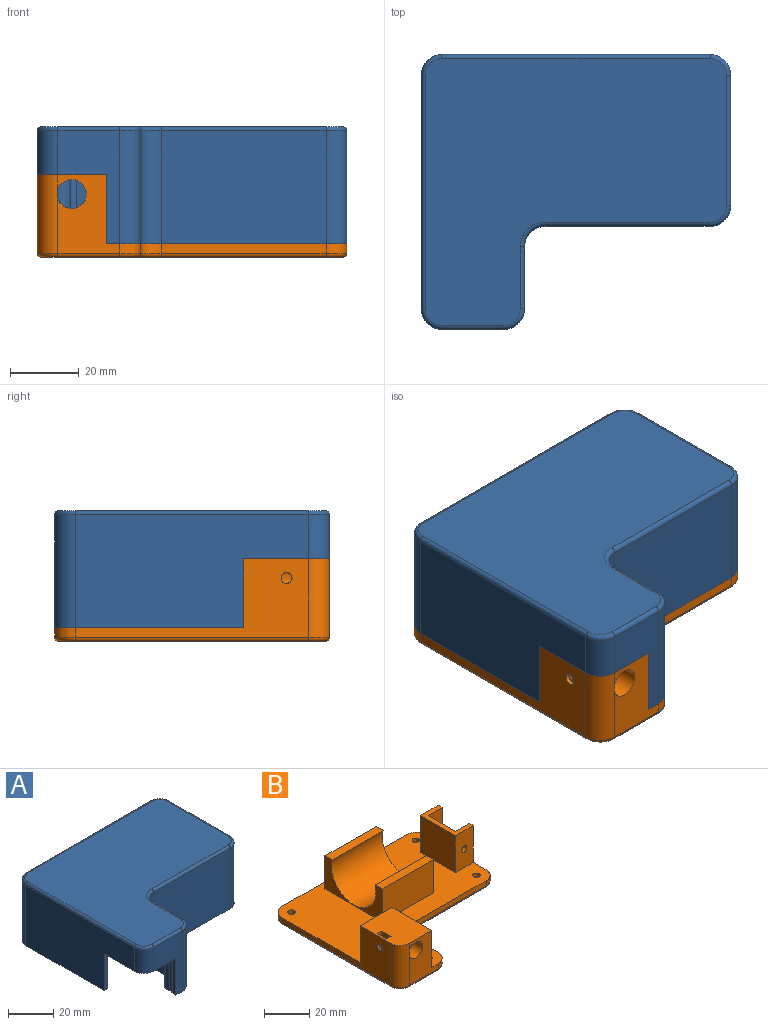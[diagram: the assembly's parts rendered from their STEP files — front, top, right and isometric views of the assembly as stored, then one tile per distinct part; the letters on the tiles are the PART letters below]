
ASSEMBLY  parts=2 mates=1
PART A: 66 faces, bbox 91x81x34 mm
  f0: plane 85.2x75.2mm, normal (0,0,-1), area 3833.6mm2, adj f15,f16,f17,f18,f19,f22,f23,f24
  f1: plane 48x32.8mm, normal (0,-1,0), area 1574.4mm2, adj f8,f13,f30,f64
  f2: plane 38x32.8mm, normal (1,0,0), area 806.4mm2, adj f8,f9,f14,f21,f28,f30,f45,f60
  f3: plane 78x32.8mm, normal (0,1,0), area 2558.4mm2, adj f9,f10,f21,f56
  f4: plane 68x32.8mm, normal (-1,0,0), area 1850.4mm2, adj f10,f11,f20,f21,f41,f55
  f5: plane 32.8x18mm, normal (0,-1,0), area 310.4mm2, adj f11,f12,f29,f30,f41,f59
  f6: plane 32.8x18mm, normal (1,0,0), area 590.4mm2, adj f12,f13,f30,f63
  f7: plane 87.6x77.6mm, normal (0,0,1), area 4984.2mm2, adj f54,f55,f56,f57,f58,f59,f60,f61
  f8: cylinder r=6mm len=32.8mm, axis (0,0,1), area 309.1mm2, adj f1,f2,f30,f62
  f9: cylinder r=6mm len=32.8mm, axis (0,0,-1), area 309.1mm2, adj f2,f3,f21,f58
  f10: cylinder r=6mm len=32.8mm, axis (0,0,1), area 309.1mm2, adj f3,f4,f21,f54
  f11: cylinder r=6mm len=12.8mm, axis (0,0,-1), area 120.6mm2, adj f4,f5,f41,f57
  f12: cylinder r=6mm len=32.8mm, axis (0,0,1), area 309.1mm2, adj f5,f6,f30,f61
  f13: cylinder r=6mm len=32.8mm, axis (0,0,-1), area 309.1mm2, adj f1,f6,f30,f65
  f14: plane 20x2.4mm, normal (0,-1,0), area 48mm2, adj f2,f15,f21,f45
  f15: plane 30x2.63mm, normal (-1,0,0), area 79mm2, adj f0,f14,f21,f31,f44
  f16: cylinder r=3.6mm len=30mm, axis (0,0,1), area 232.2mm2, adj f0,f21,f31,f32
  f17: plane 67.27x30mm, normal (0,-1,0), area 2018mm2, adj f0,f21,f32,f33
  f18: cylinder r=3.6mm len=30mm, axis (0,0,1), area 232.2mm2, adj f0,f21,f33,f34
  f19: plane 43.63x30mm, normal (1,0,0), area 1309mm2, adj f0,f20,f21,f34,f39
  f20: plane 20x2.4mm, normal (0,-1,0), area 48mm2, adj f4,f19,f21,f41
  f21: plane 90x55mm, normal (0,0,-1), area 446mm2, adj f2,f3,f4,f9,f10,f14,f15,f16
  f22: cylinder r=3.6mm len=30mm, axis (0,0,1), area 240.8mm2, adj f0,f30,f35,f38
  f23: plane 30x12.63mm, normal (-1,0,0), area 379mm2, adj f0,f24,f30,f38
  f24: cylinder r=8.4mm len=30mm, axis (0,0,1), area 395.8mm2, adj f0,f23,f25,f30
  f25: plane 42.63x30mm, normal (0,1,0), area 1279mm2, adj f0,f24,f30,f37
  f26: cylinder r=3.6mm len=30mm, axis (0,0,1), area 232.2mm2, adj f0,f30,f36,f37
  f27: plane 30x2.63mm, normal (-1,0,0), area 79mm2, adj f0,f28,f30,f36,f42
  f28: plane 20x2.4mm, normal (0,1,0), area 48mm2, adj f2,f27,f30,f45
  f29: plane 20x2.4mm, normal (-1,0,0), area 48mm2, adj f5,f30,f35,f41
  f30: plane 70x44mm, normal (0,0,-1), area 335.6mm2, adj f1,f2,f5,f6,f8,f12,f13,f22
  f31: cylinder r=2mm len=30mm, axis (0,0,1), area 111.6mm2, adj f0,f15,f16,f21
  f32: cylinder r=2mm len=30mm, axis (0,0,1), area 111.6mm2, adj f0,f16,f17,f21
  f33: cylinder r=2mm len=30mm, axis (0,0,1), area 111.6mm2, adj f0,f17,f18,f21
  f34: cylinder r=2mm len=30mm, axis (0,0,1), area 111.6mm2, adj f0,f18,f19,f21
  f35: cylinder r=2mm len=30mm, axis (0,0,-1), area 76.9mm2, adj f0,f22,f29,f30,f40
  f36: cylinder r=2mm len=30mm, axis (0,0,1), area 111.6mm2, adj f0,f26,f27,f30
  f37: cylinder r=2mm len=30mm, axis (0,0,1), area 111.6mm2, adj f0,f25,f26,f30
  f38: cylinder r=2mm len=30mm, axis (0,0,1), area 111.6mm2, adj f0,f22,f23,f30
  f39: plane 17.6x10mm, normal (0,1,0), area 176mm2, adj f0,f19,f40,f41
  f40: plane 22.6x10mm, normal (1,0,0), area 226mm2, adj f0,f35,f39,f41
  f41: plane 25x20mm, normal (0,0,-1), area 492.3mm2, adj f4,f5,f11,f20,f29,f39,f40
  f42: plane 10x8.8mm, normal (0,-1,0), area 88mm2, adj f0,f27,f43,f45
  f43: plane 22x10mm, normal (-1,0,0), area 220mm2, adj f0,f42,f44,f45
  f44: plane 10x8.8mm, normal (0,1,0), area 88mm2, adj f0,f15,f43,f45
  f45: plane 22x11.2mm, normal (0,0,-1), area 246.4mm2, adj f2,f14,f28,f42,f43,f44
  f46: cylinder r=1.1mm len=18mm, axis (0,0,-1), area 124.4mm2, adj f30,f47
  f47: cone r=0mm half-angle=59deg, axis (0,0,-1), area 4.4mm2, adj f46
  f48: cylinder r=1.1mm len=18mm, axis (0,0,-1), area 124.4mm2, adj f21,f49
  f49: cone r=0mm half-angle=59deg, axis (0,0,-1), area 4.4mm2, adj f48
  f50: cylinder r=1.1mm len=18mm, axis (0,0,-1), area 124.4mm2, adj f30,f51
  f51: cone r=0mm half-angle=59deg, axis (0,0,-1), area 4.4mm2, adj f50
  f52: cylinder r=1.1mm len=18mm, axis (0,0,-1), area 124.4mm2, adj f21,f53
  f53: cone r=0mm half-angle=59deg, axis (0,0,-1), area 4.4mm2, adj f52
  f54: torus R=4.8mm, axis (0,0,1), area 16.5mm2, adj f7,f10,f55,f56
  f55: cylinder r=1.2mm len=68mm, axis (0,1,0), area 128.2mm2, adj f4,f7,f54,f57
  f56: cylinder r=1.2mm len=78mm, axis (1,0,0), area 147mm2, adj f3,f7,f54,f58
  f57: torus R=4.8mm, axis (0,0,1), area 16.5mm2, adj f7,f11,f55,f59
  f58: torus R=4.8mm, axis (0,0,1), area 16.5mm2, adj f7,f9,f56,f60
  f59: cylinder r=1.2mm len=18mm, axis (-1,0,0), area 33.9mm2, adj f5,f7,f57,f61
  f60: cylinder r=1.2mm len=38mm, axis (0,-1,0), area 71.6mm2, adj f2,f7,f58,f62
  f61: torus R=4.8mm, axis (0,0,1), area 16.5mm2, adj f7,f12,f59,f63
  f62: torus R=4.8mm, axis (0,0,1), area 16.5mm2, adj f7,f8,f60,f64
  f63: cylinder r=1.2mm len=18mm, axis (0,-1,0), area 33.9mm2, adj f6,f7,f61,f65
  f64: cylinder r=1.2mm len=48mm, axis (-1,0,0), area 90.5mm2, adj f1,f7,f62,f65
  f65: torus R=7.2mm, axis (0,0,1), area 19.1mm2, adj f7,f13,f63,f64
PART B: 62 faces, bbox 91x81x24 mm
  f0: plane 90x80mm, normal (0,0,1), area 3444.2mm2, adj f3,f4,f5,f6,f7,f8,f9,f10
  f1: plane 17.2x8.8mm, normal (0,0,1), area 151.4mm2, adj f6,f34,f35,f36
  f2: plane 32x4.47mm, normal (0,0,1), area 143.1mm2, adj f3,f4,f12,f15
  f3: plane 36x18mm, normal (1,0,0), area 240.4mm2, adj f0,f2,f12,f13,f14,f15
  f4: plane 36x18mm, normal (-1,0,0), area 240.4mm2, adj f0,f2,f12,f13,f14,f15
  f5: plane 48x2.8mm, normal (0,-1,0), area 134.4mm2, adj f0,f27,f32,f58
  f6: plane 38x22.8mm, normal (1,0,0), area 202.4mm2, adj f0,f1,f27,f28,f33,f34,f36,f37
  f7: plane 78x2.8mm, normal (0,1,0), area 218.4mm2, adj f0,f28,f29,f50
  f8: plane 68x22.8mm, normal (-1,0,0), area 562.4mm2, adj f0,f17,f18,f25,f29,f30,f53
  f9: plane 22.8x18mm, normal (0,-1,0), area 274.1mm2, adj f0,f16,f18,f19,f30,f31,f57
  f10: plane 18x2.8mm, normal (1,0,0), area 50.4mm2, adj f0,f31,f32,f61
  f11: plane 87.6x77.6mm, normal (0,0,-1), area 4842.3mm2, adj f43,f45,f47,f49,f50,f51,f52,f53
  f12: plane 32x18mm, normal (0,1,0), area 576mm2, adj f0,f2,f3,f4
  f13: plane 32x18mm, normal (0,-1,0), area 576mm2, adj f0,f3,f4,f14
  f14: plane 32x4.47mm, normal (0,0,1), area 143.1mm2, adj f3,f4,f13,f15
  f15: cylinder r=14mm len=32mm, axis (1,0,0), area 1640.5mm2, adj f2,f3,f4,f14
  f16: plane 25x20mm, normal (1,0,0), area 500mm2, adj f0,f9,f17,f18
  f17: plane 20x20mm, normal (0,1,0), area 343.3mm2, adj f0,f8,f16,f18,f19
  f18: plane 25x20mm, normal (0,0,1), area 476mm2, adj f8,f9,f16,f17,f20,f21,f22,f23
  f19: cylinder r=4.25mm len=25mm, axis (0,-1,0), area 659.4mm2, adj f9,f17,f26,f30
  f20: plane 12x5.8mm, normal (-1,0,0), area 61.6mm2, adj f18,f21,f23,f24,f26
  f21: plane 12x2.8mm, normal (0,-1,0), area 33.6mm2, adj f18,f20,f22,f24
  f22: plane 12x5.8mm, normal (1,0,0), area 61.6mm2, adj f18,f21,f23,f24,f25
  f23: plane 12x2.8mm, normal (0,1,0), area 33.6mm2, adj f18,f20,f22,f24
  f24: plane 5.8x2.8mm, normal (0,0,1), area 16.2mm2, adj f20,f21,f22,f23
  f25: cylinder r=1.6mm len=3.2mm, axis (-1,0,0), area 12.1mm2, adj f8,f22
  f26: cylinder r=1.6mm len=3.2mm, axis (-1,0,0), area 19.1mm2, adj f19,f20
  f27: cylinder r=6mm len=6mm, axis (0,0,1), area 26.4mm2, adj f0,f5,f6,f56
  f28: cylinder r=6mm len=6mm, axis (0,0,-1), area 26.4mm2, adj f0,f6,f7,f52
  f29: cylinder r=6mm len=6mm, axis (0,0,1), area 26.4mm2, adj f0,f7,f8,f51
  f30: cylinder r=6mm len=22.8mm, axis (0,0,-1), area 214.4mm2, adj f8,f9,f18,f19,f55
  f31: cylinder r=6mm len=6mm, axis (0,0,1), area 26.4mm2, adj f0,f9,f10,f59
  f32: cylinder r=6mm len=6mm, axis (0,0,-1), area 26.4mm2, adj f0,f5,f10,f60
  f33: plane 20x11.2mm, normal (0,-1,0), area 216mm2, adj f0,f6,f38,f39,f41
  f34: plane 20x8.8mm, normal (0,1,0), area 168mm2, adj f1,f6,f35,f39,f41
  f35: plane 20x17.2mm, normal (1,0,0), area 344mm2, adj f1,f34,f36,f39
  f36: plane 20x8.8mm, normal (0,-1,0), area 168mm2, adj f1,f6,f35,f39,f40
  f37: plane 20x11.2mm, normal (0,1,0), area 216mm2, adj f0,f6,f38,f39,f40
  f38: plane 22x20mm, normal (-1,0,0), area 440mm2, adj f0,f33,f37,f39
  f39: plane 22x11.2mm, normal (0,0,1), area 95mm2, adj f6,f33,f34,f35,f36,f37,f38
  f40: cylinder r=1.6mm len=3.2mm, axis (0,-1,0), area 24.1mm2, adj f36,f37
  f41: cylinder r=1.6mm len=3.2mm, axis (0,-1,0), area 24.1mm2, adj f33,f34
  f42: cylinder r=1.65mm len=3.3mm, axis (0,0,-1), area 23.7mm2, adj f0,f43
  f43: cone r=1.65mm half-angle=45deg, axis (0,0,-1), area 38.1mm2, adj f11,f42
  f44: cylinder r=1.65mm len=3.3mm, axis (0,0,-1), area 23.7mm2, adj f0,f45
  f45: cone r=1.65mm half-angle=45deg, axis (0,0,-1), area 38.1mm2, adj f11,f44
  f46: cylinder r=1.65mm len=3.3mm, axis (0,0,-1), area 23.7mm2, adj f0,f47
  f47: cone r=1.65mm half-angle=45deg, axis (0,0,-1), area 38.1mm2, adj f11,f46
  f48: cylinder r=1.65mm len=3.3mm, axis (0,0,-1), area 23.7mm2, adj f0,f49
  f49: cone r=1.65mm half-angle=45deg, axis (0,0,-1), area 38.1mm2, adj f11,f48
  f50: cylinder r=1.2mm len=78mm, axis (-1,0,0), area 147mm2, adj f7,f11,f51,f52
  f51: torus R=4.8mm, axis (0,0,1), area 16.5mm2, adj f11,f29,f50,f53
  f52: torus R=4.8mm, axis (0,0,1), area 16.5mm2, adj f11,f28,f50,f54
  f53: cylinder r=1.2mm len=68mm, axis (0,-1,0), area 128.2mm2, adj f8,f11,f51,f55
  f54: cylinder r=1.2mm len=38mm, axis (0,1,0), area 71.6mm2, adj f6,f11,f52,f56
  f55: torus R=4.8mm, axis (0,0,1), area 16.5mm2, adj f11,f30,f53,f57
  f56: torus R=4.8mm, axis (0,0,1), area 16.5mm2, adj f11,f27,f54,f58
  f57: cylinder r=1.2mm len=18mm, axis (1,0,0), area 33.9mm2, adj f9,f11,f55,f59
  f58: cylinder r=1.2mm len=48mm, axis (1,0,0), area 90.5mm2, adj f5,f11,f56,f60
  f59: torus R=4.8mm, axis (0,0,1), area 16.5mm2, adj f11,f31,f57,f61
  f60: torus R=7.2mm, axis (0,0,1), area 19.1mm2, adj f11,f32,f58,f61
  f61: cylinder r=1.2mm len=18mm, axis (0,1,0), area 33.9mm2, adj f10,f11,f59,f60
PLACE A t=(0,0,34)mm
PLACE B at identity
MATE fastened A.f12 <-> B.f31  axis (0,0,-1) through (-21,-34,4)mm
